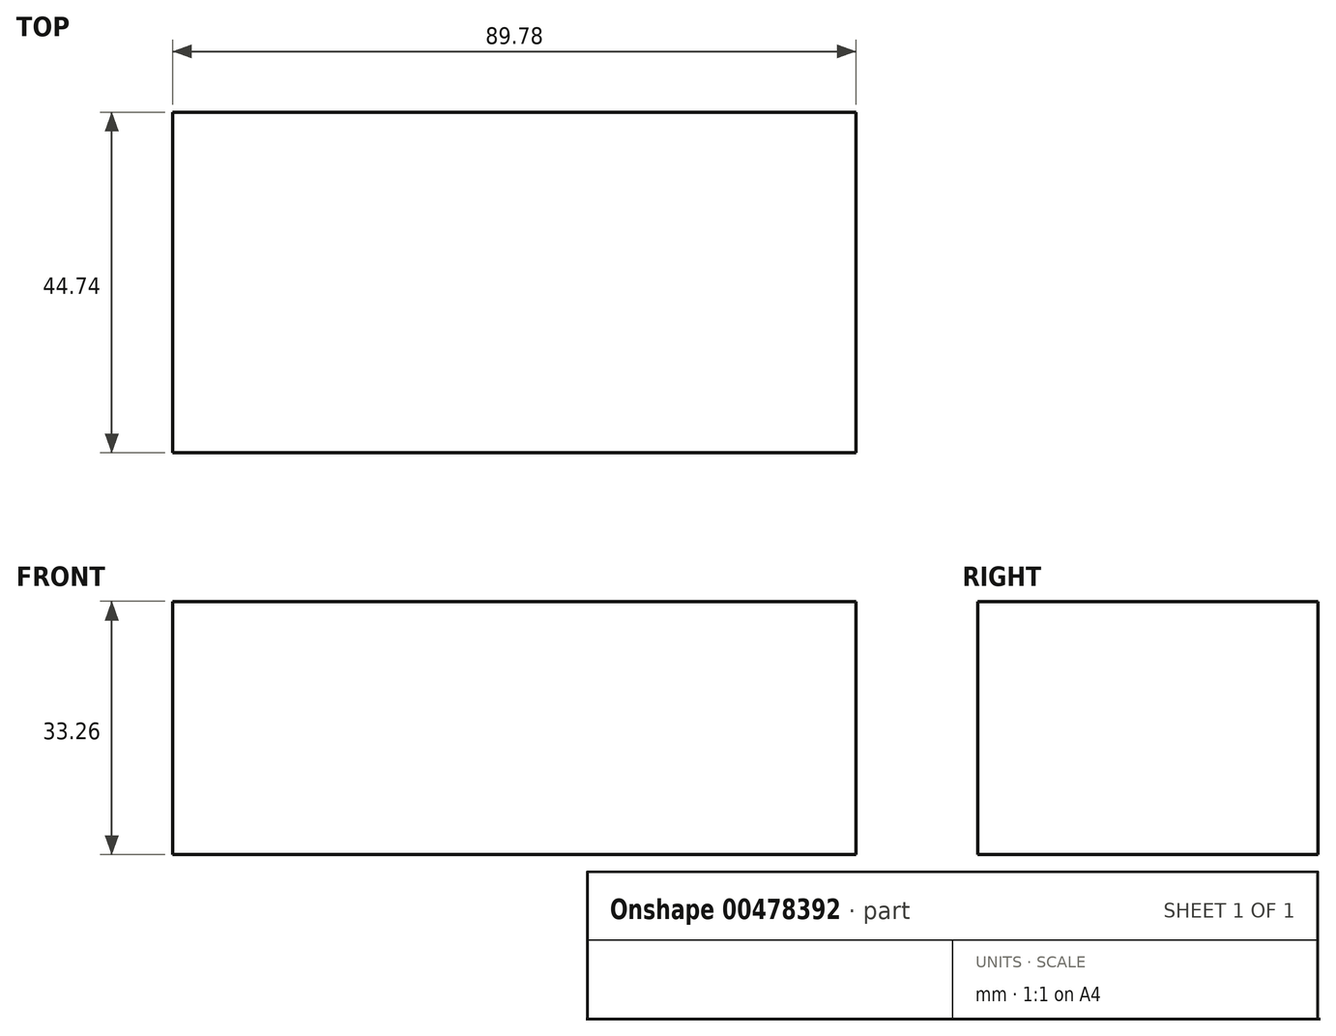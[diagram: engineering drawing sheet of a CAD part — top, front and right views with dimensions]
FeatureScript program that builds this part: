
annotation { "Feature Type Name" : "Feature", "Feature Type Description" : "" }
export const myFeature = defineFeature(function(context is Context, id is Id, definition is map)
    precondition{}
    {
        {
            var Q0;
            Q0=qCreatedBy(makeId("Front.planeOp"),FACE);
            var sketch = newSketch(context, id + "F0", { "sketchPlane" : qUnion([Q0])});
            skArc(sketch, "E0", {"start": v(-13.96, -22.83) * mm, "mid": v(-35.61, -1.45) * mm, "end": v(-57.55, -22.54) * mm});
            skLineSegment(sketch, "E1", {"start": v(-13.96, -22.83) * mm, "end": v(50.42, -22.83) * mm});
            skArc(sketch, "E2", {"start": v(95.03, -22.83) * mm, "mid": v(72.72, -1.01) * mm, "end": v(50.42, -22.83) * mm});
            skSolve(sketch);
        }
        {
            var Q0;
            Q0=sQuery(id+"F0.wireOp",EDGE,"E1");
            extrude(context, id + "F1", {"bodyType" : ToolBodyType.SURFACE, "surfaceEntities" : qUnion([Q0]), "depth" : 44.74 * mm});
        }
        {
            var Q0;
            Q0=makeQuery(id+"F1.opExtrude","SWEPT_FACE",FACE,{"disambiguationData":[OSD([sQuery(id+"F0.wireOp",EDGE,"E1")])]});
            extrude(context, id + "F2", {"entities" : qUnion([Q0]), "depth" : 33.25 * mm});
        }
        {
            var Q0;
            Q0=makeQuery(id+"F2.opExtrude","SWEPT_FACE",FACE,{"disambiguationData":[OSD([sQuery(id+"F0.wireOp",VERTEX,"E1.end")])]});
            extrude(context, id + "F3", {"entities" : qUnion([Q0]), "operationType" : NewBodyOperationType.ADD, "depth" : 25.4 * mm});
        }
    });
